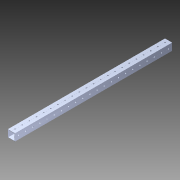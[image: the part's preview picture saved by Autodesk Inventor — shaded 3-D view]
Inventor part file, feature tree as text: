
AUTODESK INVENTOR PART (.ipt)
format: ipt  version: 2014 SP1 (Build 180222100, 222)  size: 1,854,464 bytes
history: native  units: in
note: dims shown in document units (in); Inventor stores cm internally (conversion verified against a paired STEP export)
features: extrude x5, sketch x5, mirror x2, pattern_circular x1, other x1, imported_body x1
ambient origin geometry x8: Origin, YZ Plane, XZ Plane, XY Plane, X Axis, Y Axis, Z Axis, Center Point
bodies: Body1 (feature_tree)
feature tree (15):
  pattern_circular  "CirPattern2"
  other  "1x1 tube1"
  extrude  "Extrusion1"  Depth=16.0in TaperAngle=0.0deg
  mirror  "Mirror1"
  extrude  "Extrusion2"  Depth=1.0in TaperAngle=0.0deg
  extrude  "Extrusion3"  [1 undecoded]
  extrude  "Extrusion4"  [1 undecoded]
  mirror  "Mirror2"
  extrude  "Extrusion5"  [1 undecoded]
  imported_body  "Base1"
  sketch  "Sketch1"  dims[d0=38.0in d1=0.0in d2=16.0in d3=0.0in]
  sketch  "Sketch3"  dims[d4=1.0in d5=0.0in d6=4.0in d7=0.0in]
  sketch  "Sketch4"  dims[d8=20.0in d9=0.0in]
  sketch  "Sketch5"
  sketch  "Sketch6"
note: 3 required parameter values undecoded (feature->parameter linkage not recoverable at this tier; creation-order binding heuristic only, values carry confidence <= 0.55)
